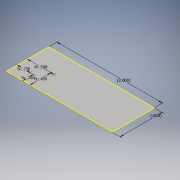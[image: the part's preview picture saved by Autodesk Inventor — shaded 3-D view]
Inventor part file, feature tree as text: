
AUTODESK INVENTOR PART (.ipt)
format: ipt  version: 2016 (Build 200138000, 138)  size: 99,328 bytes
history: native  units: in
note: dims shown in document units (in); Inventor stores cm internally (conversion verified against a paired STEP export)
features: sketch x2, extrude x1
ambient origin geometry x8: Origin, YZ Plane, XZ Plane, XY Plane, X Axis, Y Axis, Z Axis, Center Point
bodies: Solid1 (feature_tree)
feature tree (3):
  extrude  "Extrusion1"  Depth=0.8in
  sketch  "Sketch2"  dims[d2=0.01in d3=0.0in d4=2.0in d7=0.8in d9=0.5in d10=0.4in d11=0.2in d12=0.25in]
  sketch  "Sketch1"  dims[d0=2.0in d1=0.8in]
